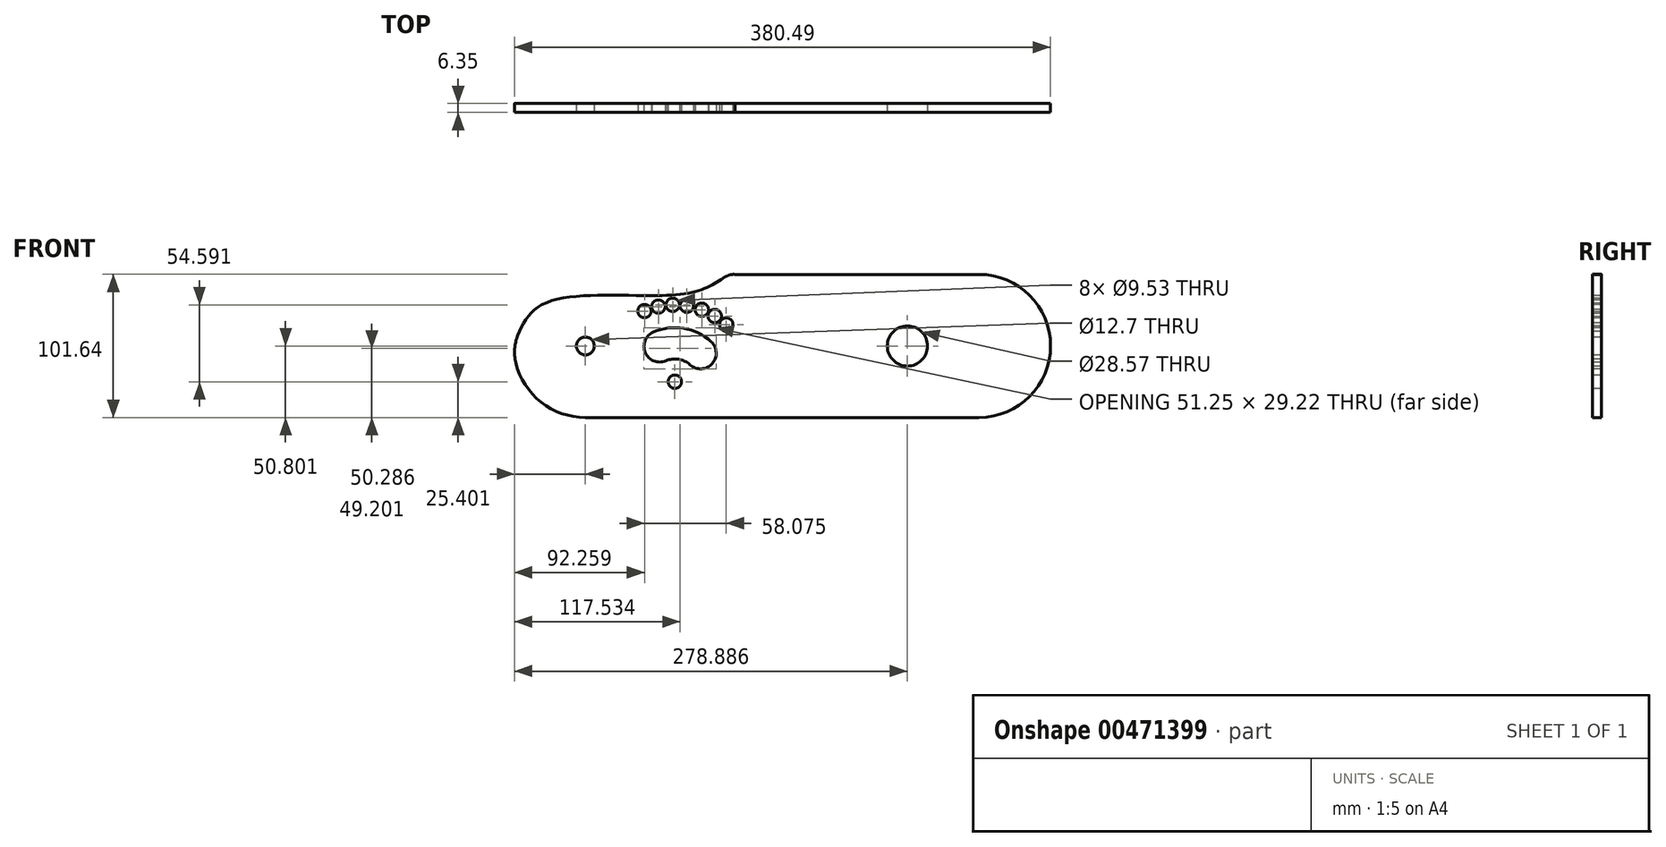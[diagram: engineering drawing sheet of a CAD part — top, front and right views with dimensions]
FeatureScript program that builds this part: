
annotation { "Feature Type Name" : "Feature", "Feature Type Description" : "" }
export const myFeature = defineFeature(function(context is Context, id is Id, definition is map)
    precondition{}
    {
        {
            var Q0;
            Q0=qCreatedBy(makeId("Front.planeOp"),FACE);
            var sketch = newSketch(context, id + "F0", { "sketchPlane" : qUnion([Q0])});
            skLineSegment(sketch, "E0.bottom", {"start": v(-37, -78.85) * mm, "end": v(138.05, -78.85) * mm});
            skLineSegment(sketch, "E0.top", {"start": v(-141.35, 22.75) * mm, "end": v(138.05, 22.75) * mm});
            skLineSegment(sketch, "E1", {"start": v(-192.15, -28.05) * mm, "end": v(188.85, -28.05) * mm, "construction": true});
            skLineSegment(sketch, "E2", {"start": v(-1.65, 22.75) * mm, "end": v(-1.65, -78.85) * mm, "construction": true});
            skCircle(sketch, "E3", {"center": v(138.05, -28.05) * mm, "radius": 50.8 * mm});
            skArc(sketch, "E4", {"start": v(-105.37, -63.9) * mm, "mid": v(-121.96, 18.9) * mm, "end": v(-192.15, -28.05) * mm});
            skFitSpline(sketch, "E5", {"points": [v(-192.15, -28.05) * mm, v(-168.86, -58.86) * mm, v(-72.24, -64.93) * mm, v(-39.87, -78.85) * mm], "startDerivative": vector(47.43, -131.99) * mm, "endDerivative": vector(91.44, -65.54) * mm});
            skLineSegment(sketch, "E6", {"start": v(-141.35, 22.75) * mm, "end": v(-141.35, -28.05) * mm, "construction": true});
            skLineSegment(sketch, "E7", {"start": v(138.05, 22.75) * mm, "end": v(138.05, -28.05) * mm, "construction": true});
            skLineSegment(sketch, "E8", {"start": v(138.05, -78.85) * mm, "end": v(138.05, -28.05) * mm, "construction": true});
            skPoint(sketch, "E9", {"position": v(-105.37, -63.9) * mm});
            skCircle(sketch, "E10", {"center": v(-141.35, -28.05) * mm, "radius": 6.35 * mm});
            skPoint(sketch, "E11", {"position": v(-77.85, -2.65) * mm});
            skCircle(sketch, "E12", {"center": v(-77.85, -2.65) * mm, "radius": 4.76 * mm});
            skArc(sketch, "E13", {"start": v(-126.2, 22.75) * mm, "mid": v(-126.71, 21.75) * mm, "end": v(-127.2, 20.74) * mm});
            skCircle(sketch, "E14", {"center": v(-58.68, -53.78) * mm, "radius": 4.76 * mm});
            skCircle(sketch, "E15", {"center": v(-49.45, -49.3) * mm, "radius": 4.76 * mm});
            skCircle(sketch, "E16", {"center": v(-69.33, -56.59) * mm, "radius": 4.76 * mm});
            skCircle(sketch, "E17", {"center": v(-41.3, -43.23) * mm, "radius": 4.76 * mm});
            skCircle(sketch, "E18", {"center": v(-79.31, -57.24) * mm, "radius": 4.76 * mm});
            skCircle(sketch, "E19", {"center": v(-89.5, -56) * mm, "radius": 4.76 * mm});
            skCircle(sketch, "E20", {"center": v(-99.38, -52.84) * mm, "radius": 4.76 * mm});
            skLineSegment(sketch, "E21", {"start": v(-77.85, -2.65) * mm, "end": v(-41.3, -43.23) * mm, "construction": true});
            skLineSegment(sketch, "E22", {"start": v(-77.85, -2.65) * mm, "end": v(-49.45, -49.3) * mm, "construction": true});
            skLineSegment(sketch, "E23", {"start": v(-77.85, -2.65) * mm, "end": v(-58.68, -53.78) * mm, "construction": true});
            skLineSegment(sketch, "E24", {"start": v(-77.85, -2.65) * mm, "end": v(-69.33, -56.59) * mm, "construction": true});
            skLineSegment(sketch, "E25", {"start": v(-77.85, -2.65) * mm, "end": v(-79.31, -57.24) * mm, "construction": true});
            skLineSegment(sketch, "E26", {"start": v(-77.85, -2.65) * mm, "end": v(-89.5, -56) * mm, "construction": true});
            skLineSegment(sketch, "E27", {"start": v(-77.85, -2.65) * mm, "end": v(-99.38, -52.84) * mm, "construction": true});
            skPoint(sketch, "E28", {"position": v(-59.58, -22.94) * mm});
            skPoint(sketch, "E29", {"position": v(-88.62, -27.74) * mm});
            skPoint(sketch, "E30", {"position": v(-83.68, -29.33) * mm});
            skPoint(sketch, "E31", {"position": v(-78.58, -29.94) * mm});
            skPoint(sketch, "E32", {"position": v(-73.6, -29.62) * mm});
            skPoint(sketch, "E33", {"position": v(-68.27, -28.22) * mm});
            skPoint(sketch, "E34", {"position": v(-63.65, -25.97) * mm});
            skCircle(sketch, "E35", {"center": v(-88.62, -27.74) * mm, "radius": 11.11 * mm});
            skCircle(sketch, "E36", {"center": v(-59.58, -22.94) * mm, "radius": 11.11 * mm});
            skArc(sketch, "E37", {"start": v(-84.24, -17.53) * mm, "mid": v(-75.21, -18.62) * mm, "end": v(-67.02, -14.68) * mm});
            skArc(sketch, "E38", {"start": v(-93, -37.96) * mm, "mid": v(-71.58, -40.55) * mm, "end": v(-52.14, -31.2) * mm});
            skArc(sketch, "E39.trimOffspring", {"start": v(-126.2, -28.05) * mm, "mid": v(-52.45, -51) * mm, "end": v(-29.51, 22.75) * mm});
            skFitSpline(sketch, "E40", {"points": [v(-44.93, -75.3) * mm, v(-35.19, -78.85) * mm, v(-7.4, -62.79) * mm], "startDerivative": vector(23.89, -16.09) * mm, "endDerivative": vector(48.9, 36.33) * mm});
            skCircle(sketch, "E41", {"center": v(87.25, -28.05) * mm, "radius": 14.29 * mm});
            skSolve(sketch);
        }
        {
            var Q0;
            Q0 = qSketchRegion(id + "F0", true);
            extrude(context, id + "F1", {"entities" : qUnion([Q0]), "depth" : 6.35 * mm});
        }
        {
            var Q0;
            Q0=makeQuery(id+"F1.opExtrude","SWEPT_EDGE",EDGE,{"disambiguationData":[OSD([sQuery(id+"F0.wireOp",EDGE,"E4"),sQuery(id+"F0.wireOp",EDGE,"E5")])]});
            fillet(context, id + "F2", {"entities" : qUnion([Q0]), "radius" : 32.04 * mm, "tangentPropagation" : true, "allowEdgeOverflow" : false});
        }
        {
            var Q0;
            Q0=makeQuery(id+"F1.opExtrude","SWEPT_BODY",BODY,{"disambiguationData":[OSD([sQuery(id+"F0.wireOp",EDGE,"E0.bottom"),sQuery(id+"F0.wireOp",EDGE,"E0.top"),sQuery(id+"F0.wireOp",EDGE,"E3"),sQuery(id+"F0.wireOp",EDGE,"E4"),sQuery(id+"F0.wireOp",EDGE,"E5"),sQuery(id+"F0.wireOp",EDGE,"E10"),sQuery(id+"F0.wireOp",EDGE,"E12"),sQuery(id+"F0.wireOp",EDGE,"E14"),sQuery(id+"F0.wireOp",EDGE,"E15"),sQuery(id+"F0.wireOp",EDGE,"E16"),sQuery(id+"F0.wireOp",EDGE,"E17"),sQuery(id+"F0.wireOp",EDGE,"E18"),sQuery(id+"F0.wireOp",EDGE,"E19"),sQuery(id+"F0.wireOp",EDGE,"E20"),sQuery(id+"F0.wireOp",EDGE,"E35"),sQuery(id+"F0.wireOp",EDGE,"E36"),sQuery(id+"F0.wireOp",EDGE,"E37"),sQuery(id+"F0.wireOp",EDGE,"E38"),sQuery(id+"F0.wireOp",EDGE,"E40"),sQuery(id+"F0.wireOp",EDGE,"E41")])]});
            var Q1;
            Q1=makeQuery(id+"F1.opExtrude","CAP_EDGE",EDGE,{"disambiguationData":[OSD([sQuery(id+"F0.wireOp",EDGE,"E0.top")])],"isStart":false});
            transform(context, id + "F3", {"entities" : qUnion([Q0]), "transformType" : TransformType.ROTATION, "transformAxis" : qUnion([Q1]), "angle" : 180 * degree, "makeCopy" : false});
        }
    });
